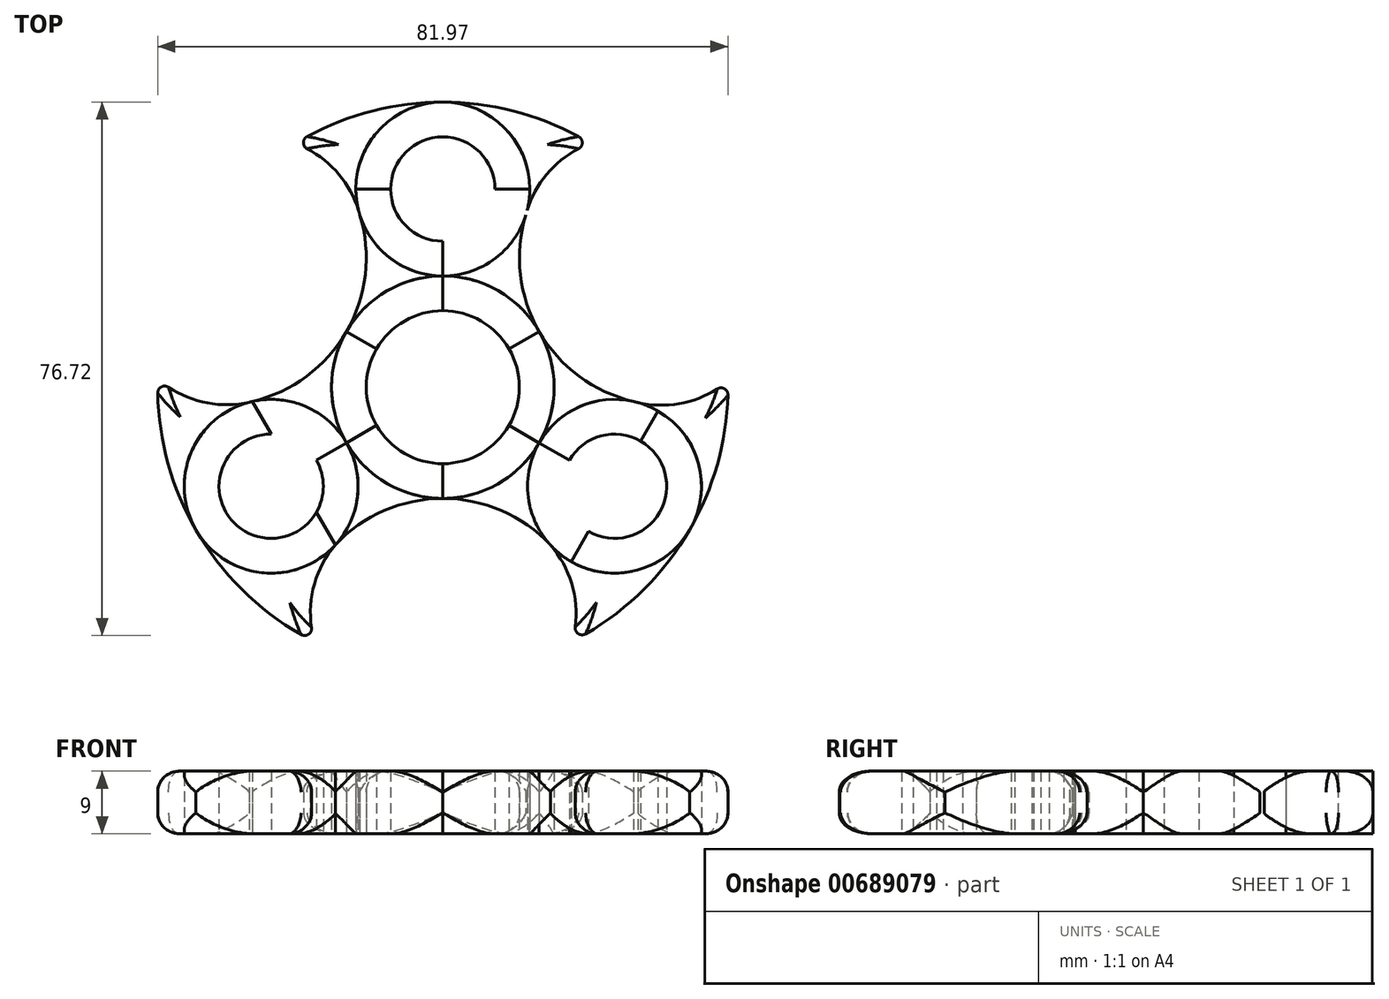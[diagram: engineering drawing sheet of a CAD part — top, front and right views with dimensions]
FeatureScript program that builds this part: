
annotation { "Feature Type Name" : "Feature", "Feature Type Description" : "" }
export const myFeature = defineFeature(function(context is Context, id is Id, definition is map)
    precondition{}
    {
        {
            var Q0;
            Q0=qCreatedBy(makeId("Top.planeOp"),FACE);
            var sketch = newSketch(context, id + "F0", { "sketchPlane" : qUnion([Q0])});
            skCircle(sketch, "E0", {"center": v(0, 0) * mm, "radius": 11 * mm});
            skLineSegment(sketch, "E1", {"start": v(0, 11) * mm, "end": v(-9.53, -5.5) * mm});
            skLineSegment(sketch, "E2", {"start": v(-9.53, -5.5) * mm, "end": v(9.53, -5.5) * mm});
            skLineSegment(sketch, "E3", {"start": v(9.53, -5.5) * mm, "end": v(0, 11) * mm});
            skCircle(sketch, "E4", {"center": v(0, 0) * mm, "radius": 16 * mm});
            skLineSegment(sketch, "E5", {"start": v(0, 11) * mm, "end": v(0, 21) * mm});
            skLineSegment(sketch, "E6", {"start": v(-9.53, -5.5) * mm, "end": v(4.76, 2.75) * mm});
            skLineSegment(sketch, "E7", {"start": v(0, -5.5) * mm, "end": v(0, 11) * mm});
            skLineSegment(sketch, "E8", {"start": v(-4.76, 2.75) * mm, "end": v(9.53, -5.5) * mm});
            skLineSegment(sketch, "E9", {"start": v(0, 0) * mm, "end": v(-18.19, -10.5) * mm});
            skLineSegment(sketch, "E10", {"start": v(0, 0) * mm, "end": v(18.19, -10.5) * mm});
            skLineSegment(sketch, "E11", {"start": v(-18.19, -10.5) * mm, "end": v(-24.68, -14.25) * mm});
            skCircle(sketch, "E12", {"center": v(-24.68, -14.25) * mm, "radius": 7.5 * mm});
            skCircle(sketch, "E13", {"center": v(-24.68, -14.25) * mm, "radius": 12.5 * mm});
            skLineSegment(sketch, "E14", {"start": v(0, 21) * mm, "end": v(0, 28.5) * mm});
            skCircle(sketch, "E15", {"center": v(0, 28.5) * mm, "radius": 7.5 * mm});
            skCircle(sketch, "E16", {"center": v(0, 28.5) * mm, "radius": 12.5 * mm});
            skLineSegment(sketch, "E17", {"start": v(-18.19, -10.5) * mm, "end": v(-9.53, -5.5) * mm});
            skCircle(sketch, "E18", {"center": v(24.68, -14.25) * mm, "radius": 7.5 * mm});
            skCircle(sketch, "E19", {"center": v(24.68, -14.25) * mm, "radius": 12.5 * mm});
            skLineSegment(sketch, "E20", {"start": v(9.53, -5.5) * mm, "end": v(18.19, -10.5) * mm});
            skArc(sketch, "E21", {"start": v(-41, -0.85) * mm, "mid": v(-35.25, -20.94) * mm, "end": v(-20.37, -35.58) * mm});
            skLineSegment(sketch, "E22", {"start": v(0, 0) * mm, "end": v(24.68, -14.25) * mm});
            skLineSegment(sketch, "E23", {"start": v(24.68, -14.25) * mm, "end": v(18.43, -25.08) * mm});
            skLineSegment(sketch, "E24", {"start": v(18.43, -25.08) * mm, "end": v(30.93, -3.42) * mm});
            skLineSegment(sketch, "E25", {"start": v(0, 28.5) * mm, "end": v(12.5, 28.5) * mm});
            skLineSegment(sketch, "E26", {"start": v(12.5, 28.5) * mm, "end": v(-12.5, 28.5) * mm});
            skLineSegment(sketch, "E27", {"start": v(-4.76, 2.75) * mm, "end": v(-13.86, 8) * mm});
            skLineSegment(sketch, "E28", {"start": v(4.76, 2.75) * mm, "end": v(13.86, 8) * mm});
            skLineSegment(sketch, "E29", {"start": v(0, -5.5) * mm, "end": v(0, -16) * mm});
            skLineSegment(sketch, "E30", {"start": v(18.19, -10.5) * mm, "end": v(24.68, -14.25) * mm});
            skLineSegment(sketch, "E31", {"start": v(-21.43, -12.38) * mm, "end": v(-27.4, -2.05) * mm});
            skLineSegment(sketch, "E32", {"start": v(-27.4, -2.05) * mm, "end": v(-18.19, -18) * mm});
            skArc(sketch, "E33", {"start": v(-39.44, 0) * mm, "mid": v(-33.63, -2.3) * mm, "end": v(-27.4, -2.05) * mm});
            skLineSegment(sketch, "E34", {"start": v(-21.43, -12.38) * mm, "end": v(-15.47, -22.7) * mm});
            skArc(sketch, "E35", {"start": v(-15.47, -22.7) * mm, "mid": v(-18.45, -28.27) * mm, "end": v(-18.88, -34.57) * mm});
            skArc(sketch, "E36", {"start": v(19.03, -34.5) * mm, "mid": v(18.52, -28.22) * mm, "end": v(15.47, -22.7) * mm});
            skArc(sketch, "E37", {"start": v(15.47, -22.7) * mm, "mid": v(0, -16) * mm, "end": v(-15.47, -22.7) * mm});
            skArc(sketch, "E38", {"start": v(27.4, -2.05) * mm, "mid": v(33.61, -2.43) * mm, "end": v(39.45, -0.25) * mm});
            skArc(sketch, "E39", {"start": v(19.5, 34.29) * mm, "mid": v(14.7, 30.32) * mm, "end": v(11.92, 24.75) * mm});
            skArc(sketch, "E40", {"start": v(-11.92, 24.75) * mm, "mid": v(-14.7, 30.32) * mm, "end": v(-19.5, 34.29) * mm});
            skArc(sketch, "E41", {"start": v(-27.4, -2.05) * mm, "mid": v(-13.86, 8) * mm, "end": v(-11.92, 24.75) * mm});
            skArc(sketch, "E42", {"start": v(11.92, 24.75) * mm, "mid": v(13.86, 8) * mm, "end": v(27.4, -2.05) * mm});
            skArc(sketch, "E43.trimOffspring", {"start": v(20.53, -35.5) * mm, "mid": v(35.23, -20.97) * mm, "end": v(40.98, -1.12) * mm});
            skArc(sketch, "E44.trimOffspring", {"start": v(19.52, 36.06) * mm, "mid": v(0, 41) * mm, "end": v(-19.52, 36.06) * mm});
            skPoint(sketch, "E45.visualSharp", {"position": v(-40.98, 1.18) * mm});
            skArc(sketch, "E45.filletArc", {"start": v(-39.44, 0) * mm, "mid": v(-40.47, 0.04) * mm, "end": v(-41, -0.85) * mm});
            skPoint(sketch, "E46.visualSharp", {"position": v(-18.43, -36.62) * mm});
            skArc(sketch, "E46.filletArc", {"start": v(-20.37, -35.58) * mm, "mid": v(-19.3, -35.54) * mm, "end": v(-18.88, -34.57) * mm});
            skPoint(sketch, "E47.visualSharp", {"position": v(18.62, -36.53) * mm});
            skArc(sketch, "E47.filletArc", {"start": v(19.03, -34.5) * mm, "mid": v(19.47, -35.46) * mm, "end": v(20.53, -35.5) * mm});
            skPoint(sketch, "E48.visualSharp", {"position": v(41, 0.87) * mm});
            skArc(sketch, "E48.filletArc", {"start": v(40.98, -1.12) * mm, "mid": v(40.48, -0.23) * mm, "end": v(39.45, -0.25) * mm});
            skPoint(sketch, "E49.visualSharp", {"position": v(21.25, 35.06) * mm});
            skArc(sketch, "E49.filletArc", {"start": v(19.5, 34.29) * mm, "mid": v(20.04, 35.17) * mm, "end": v(19.52, 36.06) * mm});
            skPoint(sketch, "E50.visualSharp", {"position": v(-21.25, 35.06) * mm});
            skArc(sketch, "E50.filletArc", {"start": v(-19.52, 36.06) * mm, "mid": v(-20.04, 35.17) * mm, "end": v(-19.5, 34.29) * mm});
            skSolve(sketch);
        }
        {
            var Q0;
            {var subQ0=sQuery(id+"F0.wireOp",EDGE,"E35");Q0=makeQuery(id+"F0.imprint","IMPRINT",FACE,{"disambiguationData":[TD([[makeQuery(id+"F0.imprint","IMPRINT",EDGE,{"derivedFrom":subQ0}),-1.0]])]});}
            var Q1;
            {var subQ1=sQuery(id+"F0.wireOp",EDGE,"E32");var subQ4=sQuery(id+"F0.wireOp",EDGE,"E12");var subQ5=makeQuery(id+"F0.imprint","INTERSECT",VERTEX,{"derivedFrom":[subQ4,subQ1]});Q1=makeQuery(id+"F0.imprint","IMPRINT",FACE,{"disambiguationData":[TD([[makeQuery(id+"F0.imprint","IMPRINT",EDGE,{"disambiguationData":[TD([[subQ5,-1.0]])],"derivedFrom":subQ4}),-1.0]])]});}
            var Q2;
            {var subQ5=sQuery(id+"F0.wireOp",EDGE,"E45.filletArc");Q2=makeQuery(id+"F0.imprint","IMPRINT",FACE,{"disambiguationData":[TD([[makeQuery(id+"F0.imprint","IMPRINT",EDGE,{"derivedFrom":subQ5}),1.0]])]});}
            var Q3;
            {var subQ1=sQuery(id+"F0.wireOp",EDGE,"E12");var subQ3=sQuery(id+"F0.wireOp",EDGE,"E32");var subQ4=makeQuery(id+"F0.imprint","INTERSECT",VERTEX,{"derivedFrom":[subQ1,subQ3]});Q3=makeQuery(id+"F0.imprint","IMPRINT",FACE,{"disambiguationData":[TD([[makeQuery(id+"F0.imprint","IMPRINT",EDGE,{"disambiguationData":[TD([[subQ4,1.0]])],"derivedFrom":subQ1}),-1.0]])]});}
            var Q4;
            {var subQ1=sQuery(id+"F0.wireOp",EDGE,"E12");var subQ3=sQuery(id+"F0.wireOp",EDGE,"E34");var subQ4=makeQuery(id+"F0.imprint","INTERSECT",VERTEX,{"derivedFrom":[subQ1,subQ3]});Q4=makeQuery(id+"F0.imprint","IMPRINT",FACE,{"disambiguationData":[TD([[makeQuery(id+"F0.imprint","IMPRINT",EDGE,{"disambiguationData":[TD([[subQ4,-1.0]])],"derivedFrom":subQ1}),-1.0]])]});}
            var Q5;
            {var subQ0=sQuery(id+"F0.wireOp",EDGE,"E37");var subQ1=sQuery(id+"F0.wireOp",EDGE,"E4");var subQ2=makeQuery(id+"F0.imprint","INTERSECT",VERTEX,{"derivedFrom":[subQ1,sQuery(id+"F0.wireOp",EDGE,"E29"),subQ0]});Q5=makeQuery(id+"F0.imprint","IMPRINT",FACE,{"disambiguationData":[TD([[makeQuery(id+"F0.imprint","IMPRINT",EDGE,{"disambiguationData":[TD([[subQ2,1.0]])],"derivedFrom":subQ1}),-1.0]])]});}
            var Q6;
            {var subQ0=sQuery(id+"F0.wireOp",EDGE,"E41");var subQ1=sQuery(id+"F0.wireOp",EDGE,"E4");var subQ2=makeQuery(id+"F0.imprint","INTERSECT",VERTEX,{"derivedFrom":[subQ1,sQuery(id+"F0.wireOp",EDGE,"E27"),subQ0]});Q6=makeQuery(id+"F0.imprint","IMPRINT",FACE,{"disambiguationData":[TD([[makeQuery(id+"F0.imprint","IMPRINT",EDGE,{"disambiguationData":[TD([[subQ2,-1.0]])],"derivedFrom":subQ1}),-1.0]])]});}
            var Q7;
            {var subQ1=sQuery(id+"F0.wireOp",EDGE,"E0");var subQ3=sQuery(id+"F0.wireOp",EDGE,"E27");var subQ4=makeQuery(id+"F0.imprint","INTERSECT",VERTEX,{"derivedFrom":[subQ1,subQ3]});Q7=makeQuery(id+"F0.imprint","IMPRINT",FACE,{"disambiguationData":[TD([[makeQuery(id+"F0.imprint","IMPRINT",EDGE,{"disambiguationData":[TD([[subQ4,-1.0]])],"derivedFrom":subQ3}),1.0]])]});}
            var Q8;
            {var subQ1=sQuery(id+"F0.wireOp",EDGE,"E0");var subQ3=sQuery(id+"F0.wireOp",EDGE,"E29");var subQ4=makeQuery(id+"F0.imprint","INTERSECT",VERTEX,{"derivedFrom":[subQ1,subQ3]});Q8=makeQuery(id+"F0.imprint","IMPRINT",FACE,{"disambiguationData":[TD([[makeQuery(id+"F0.imprint","IMPRINT",EDGE,{"disambiguationData":[TD([[subQ4,-1.0]])],"derivedFrom":subQ3}),-1.0]])]});}
            var Q9;
            {var subQ1=sQuery(id+"F0.wireOp",EDGE,"E0");var subQ3=sQuery(id+"F0.wireOp",EDGE,"E29");var subQ4=makeQuery(id+"F0.imprint","INTERSECT",VERTEX,{"derivedFrom":[subQ1,subQ3]});Q9=makeQuery(id+"F0.imprint","IMPRINT",FACE,{"disambiguationData":[TD([[makeQuery(id+"F0.imprint","IMPRINT",EDGE,{"disambiguationData":[TD([[subQ4,-1.0]])],"derivedFrom":subQ3}),1.0]])]});}
            var Q10;
            {var subQ0=sQuery(id+"F0.wireOp",EDGE,"E37");var subQ1=sQuery(id+"F0.wireOp",EDGE,"E4");var subQ2=makeQuery(id+"F0.imprint","INTERSECT",VERTEX,{"derivedFrom":[subQ1,sQuery(id+"F0.wireOp",EDGE,"E29"),subQ0]});Q10=makeQuery(id+"F0.imprint","IMPRINT",FACE,{"disambiguationData":[TD([[makeQuery(id+"F0.imprint","IMPRINT",EDGE,{"disambiguationData":[TD([[subQ2,-1.0]])],"derivedFrom":subQ1}),-1.0]])]});}
            var Q11;
            {var subQ0=sQuery(id+"F0.wireOp",EDGE,"E42");var subQ1=sQuery(id+"F0.wireOp",EDGE,"E4");var subQ2=makeQuery(id+"F0.imprint","INTERSECT",VERTEX,{"derivedFrom":[subQ1,sQuery(id+"F0.wireOp",EDGE,"E28"),subQ0]});Q11=makeQuery(id+"F0.imprint","IMPRINT",FACE,{"disambiguationData":[TD([[makeQuery(id+"F0.imprint","IMPRINT",EDGE,{"disambiguationData":[TD([[subQ2,1.0]])],"derivedFrom":subQ1}),-1.0]])]});}
            var Q12;
            {var subQ1=sQuery(id+"F0.wireOp",EDGE,"E0");var subQ3=sQuery(id+"F0.wireOp",EDGE,"E28");var subQ4=makeQuery(id+"F0.imprint","INTERSECT",VERTEX,{"derivedFrom":[subQ1,subQ3]});Q12=makeQuery(id+"F0.imprint","IMPRINT",FACE,{"disambiguationData":[TD([[makeQuery(id+"F0.imprint","IMPRINT",EDGE,{"disambiguationData":[TD([[subQ4,-1.0]])],"derivedFrom":subQ3}),-1.0]])]});}
            var Q13;
            {var subQ0=sQuery(id+"F0.wireOp",EDGE,"E36");Q13=makeQuery(id+"F0.imprint","IMPRINT",FACE,{"disambiguationData":[TD([[makeQuery(id+"F0.imprint","IMPRINT",EDGE,{"derivedFrom":subQ0}),-1.0]])]});}
            var Q14;
            {var subQ4=sQuery(id+"F0.wireOp",EDGE,"txFMtDzL-8cam-mCzZ-D6f6-VIdZ1Xnn4ipE");Q14=makeQuery(id+"F0.imprint","IMPRINT",FACE,{"disambiguationData":[TD([[makeQuery(id+"F0.imprint","IMPRINT",EDGE,{"derivedFrom":subQ4}),-1.0]])]});}
            var Q15;
            {var subQ0=sQuery(id+"F0.wireOp",EDGE,"E24");var subQ3=sQuery(id+"F0.wireOp",EDGE,"E18");var subQ7=makeQuery(id+"F0.imprint","INTERSECT",VERTEX,{"disambiguationData":[OD(0.0)],"derivedFrom":[subQ3,subQ0]});Q15=makeQuery(id+"F0.imprint","IMPRINT",FACE,{"disambiguationData":[TD([[makeQuery(id+"F0.imprint","IMPRINT",EDGE,{"disambiguationData":[TD([[subQ7,1.0]])],"derivedFrom":subQ3}),-1.0]])]});}
            var Q16;
            {var subQ3=sQuery(id+"F0.wireOp",EDGE,"E19");var subQ5=sQuery(id+"F0.wireOp",EDGE,"E24");var subQ6=makeQuery(id+"F0.imprint","INTERSECT",VERTEX,{"derivedFrom":[subQ3,subQ5]});Q16=makeQuery(id+"F0.imprint","IMPRINT",FACE,{"disambiguationData":[TD([[makeQuery(id+"F0.imprint","IMPRINT",EDGE,{"disambiguationData":[TD([[subQ6,-1.0]])],"derivedFrom":subQ5}),1.0]])]});}
            var Q17;
            {var subQ1=sQuery(id+"F0.wireOp",EDGE,"E18");var subQ5=sQuery(id+"F0.wireOp",EDGE,"E24");var subQ10=makeQuery(id+"F0.imprint","INTERSECT",VERTEX,{"disambiguationData":[OD(0.0)],"derivedFrom":[subQ1,subQ5]});Q17=makeQuery(id+"F0.imprint","IMPRINT",FACE,{"disambiguationData":[TD([[makeQuery(id+"F0.imprint","IMPRINT",EDGE,{"disambiguationData":[TD([[subQ10,-1.0]])],"derivedFrom":subQ1}),-1.0]])]});}
            var Q18;
            {var subQ1=sQuery(id+"F0.wireOp",EDGE,"E0");var subQ3=sQuery(id+"F0.wireOp",EDGE,"E27");var subQ4=makeQuery(id+"F0.imprint","INTERSECT",VERTEX,{"derivedFrom":[subQ1,subQ3]});Q18=makeQuery(id+"F0.imprint","IMPRINT",FACE,{"disambiguationData":[TD([[makeQuery(id+"F0.imprint","IMPRINT",EDGE,{"disambiguationData":[TD([[subQ4,-1.0]])],"derivedFrom":subQ3}),-1.0]])]});}
            var Q19;
            {var subQ1=sQuery(id+"F0.wireOp",EDGE,"E0");var subQ3=sQuery(id+"F0.wireOp",EDGE,"E28");var subQ4=makeQuery(id+"F0.imprint","INTERSECT",VERTEX,{"derivedFrom":[subQ1,subQ3]});Q19=makeQuery(id+"F0.imprint","IMPRINT",FACE,{"disambiguationData":[TD([[makeQuery(id+"F0.imprint","IMPRINT",EDGE,{"disambiguationData":[TD([[subQ4,-1.0]])],"derivedFrom":subQ3}),1.0]])]});}
            var Q20;
            {var subQ0=sQuery(id+"F0.wireOp",EDGE,"E41");var subQ1=sQuery(id+"F0.wireOp",EDGE,"E4");var subQ2=makeQuery(id+"F0.imprint","INTERSECT",VERTEX,{"derivedFrom":[subQ1,sQuery(id+"F0.wireOp",EDGE,"E27"),subQ0]});Q20=makeQuery(id+"F0.imprint","IMPRINT",FACE,{"disambiguationData":[TD([[makeQuery(id+"F0.imprint","IMPRINT",EDGE,{"disambiguationData":[TD([[subQ2,1.0]])],"derivedFrom":subQ1}),-1.0]])]});}
            var Q21;
            {var subQ0=sQuery(id+"F0.wireOp",EDGE,"E42");var subQ1=sQuery(id+"F0.wireOp",EDGE,"E4");var subQ2=makeQuery(id+"F0.imprint","INTERSECT",VERTEX,{"derivedFrom":[subQ1,sQuery(id+"F0.wireOp",EDGE,"E28"),subQ0]});Q21=makeQuery(id+"F0.imprint","IMPRINT",FACE,{"disambiguationData":[TD([[makeQuery(id+"F0.imprint","IMPRINT",EDGE,{"disambiguationData":[TD([[subQ2,-1.0]])],"derivedFrom":subQ1}),-1.0]])]});}
            var Q22;
            {var subQ1=sQuery(id+"F0.wireOp",EDGE,"E16");var subQ5=sQuery(id+"F0.wireOp",EDGE,"E26");var subQ6=makeQuery(id+"F0.imprint","INTERSECT",VERTEX,{"disambiguationData":[OD(1.0)],"derivedFrom":[subQ1,subQ5]});Q22=makeQuery(id+"F0.imprint","IMPRINT",FACE,{"disambiguationData":[TD([[makeQuery(id+"F0.imprint","IMPRINT",EDGE,{"disambiguationData":[TD([[subQ6,-1.0]])],"derivedFrom":subQ1}),1.0]])]});}
            var Q23;
            {var subQ0=sQuery(id+"F0.wireOp",EDGE,"E26");var subQ1=sQuery(id+"F0.wireOp",EDGE,"E16");var subQ2=makeQuery(id+"F0.imprint","INTERSECT",VERTEX,{"disambiguationData":[OD(0.0)],"derivedFrom":[subQ1,subQ0]});Q23=makeQuery(id+"F0.imprint","IMPRINT",FACE,{"disambiguationData":[TD([[makeQuery(id+"F0.imprint","IMPRINT",EDGE,{"disambiguationData":[TD([[subQ2,1.0]])],"derivedFrom":subQ1}),1.0]])]});}
            var Q24;
            {var subQ0=sQuery(id+"F0.wireOp",EDGE,"E26");var subQ3=sQuery(id+"F0.wireOp",EDGE,"E15");var subQ7=makeQuery(id+"F0.imprint","INTERSECT",VERTEX,{"disambiguationData":[OD(0.0)],"derivedFrom":[subQ3,subQ0]});Q24=makeQuery(id+"F0.imprint","IMPRINT",FACE,{"disambiguationData":[TD([[makeQuery(id+"F0.imprint","IMPRINT",EDGE,{"disambiguationData":[TD([[subQ7,1.0]])],"derivedFrom":subQ3}),-1.0]])]});}
            var Q25;
            {var subQ0=sQuery(id+"F0.wireOp",EDGE,"E49.filletArc");Q25=makeQuery(id+"F0.imprint","IMPRINT",FACE,{"disambiguationData":[TD([[makeQuery(id+"F0.imprint","IMPRINT",EDGE,{"derivedFrom":subQ0}),1.0]])]});}
            var Q26;
            {var subQ0=sQuery(id+"F0.wireOp",EDGE,"E50.filletArc");Q26=makeQuery(id+"F0.imprint","IMPRINT",FACE,{"disambiguationData":[TD([[makeQuery(id+"F0.imprint","IMPRINT",EDGE,{"derivedFrom":subQ0}),1.0]])]});}
            var Q27;
            {var subQ0=sQuery(id+"F0.wireOp",EDGE,"E48.filletArc");Q27=makeQuery(id+"F0.imprint","IMPRINT",FACE,{"disambiguationData":[TD([[makeQuery(id+"F0.imprint","IMPRINT",EDGE,{"derivedFrom":subQ0}),1.0]])]});}
            extrude(context, id + "F1", {"entities" : qUnion([Q0, Q1, Q2, Q3, Q4, Q5, Q6, Q7, Q8, Q9, Q10, Q11, Q12, Q13, Q14, Q15, Q16, Q17, Q18, Q19, Q20, Q21, Q22, Q23, Q24, Q25, Q26, Q27]), "depth" : 9 * mm, "offsetDistance" : 25 * mm});
        }
        {
            var Q0;
            Q0=makeQuery(id+"F1.opExtrude","CAP_EDGE",EDGE,{"disambiguationData":[OSD([sQuery(id+"F0.wireOp",EDGE,"E44.trimOffspring")])],"isStart":false});
            var Q1;
            Q1=makeQuery(id+"F1.opExtrude","CAP_EDGE",EDGE,{"disambiguationData":[OSD([sQuery(id+"F0.wireOp",EDGE,"E43.trimOffspring")])],"isStart":false});
            var Q2;
            Q2=makeQuery(id+"F1.opExtrude","CAP_EDGE",EDGE,{"disambiguationData":[OSD([sQuery(id+"F0.wireOp",EDGE,"E21")])],"isStart":false});
            var Q3;
            Q3=makeQuery(id+"F1.opExtrude","CAP_EDGE",EDGE,{"disambiguationData":[OSD([sQuery(id+"F0.wireOp",EDGE,"E42")])],"isStart":false});
            var Q4;
            Q4=makeQuery(id+"F1.opExtrude","CAP_EDGE",EDGE,{"disambiguationData":[OSD([sQuery(id+"F0.wireOp",EDGE,"E37")])],"isStart":false});
            var Q5;
            Q5=makeQuery(id+"F1.opExtrude","CAP_EDGE",EDGE,{"disambiguationData":[OSD([sQuery(id+"F0.wireOp",EDGE,"E41")])],"isStart":false});
            fillet(context, id + "F2", {"entities" : qUnion([Q0, Q1, Q2, Q3, Q4, Q5]), "radius" : 3 * mm, "tangentPropagation" : true, "allowEdgeOverflow" : false});
        }
        {
            var Q0;
            Q0=makeQuery(id+"F1.opExtrude","CAP_EDGE",EDGE,{"disambiguationData":[OSD([sQuery(id+"F0.wireOp",EDGE,"E44.trimOffspring")])],"isStart":true});
            var Q1;
            Q1=makeQuery(id+"F1.opExtrude","CAP_EDGE",EDGE,{"disambiguationData":[OSD([sQuery(id+"F0.wireOp",EDGE,"E21")])],"isStart":true});
            var Q2;
            Q2=makeQuery(id+"F1.opExtrude","CAP_EDGE",EDGE,{"disambiguationData":[OSD([sQuery(id+"F0.wireOp",EDGE,"E43.trimOffspring")])],"isStart":true});
            var Q3;
            Q3=makeQuery(id+"F1.opExtrude","CAP_EDGE",EDGE,{"disambiguationData":[OSD([sQuery(id+"F0.wireOp",EDGE,"E37")])],"isStart":true});
            var Q4;
            Q4=makeQuery(id+"F1.opExtrude","CAP_EDGE",EDGE,{"disambiguationData":[OSD([sQuery(id+"F0.wireOp",EDGE,"E42")])],"isStart":true});
            fillet(context, id + "F3", {"entities" : qUnion([Q0, Q1, Q2, Q3, Q4]), "radius" : 3 * mm, "tangentPropagation" : true, "allowEdgeOverflow" : false});
        }
    });
